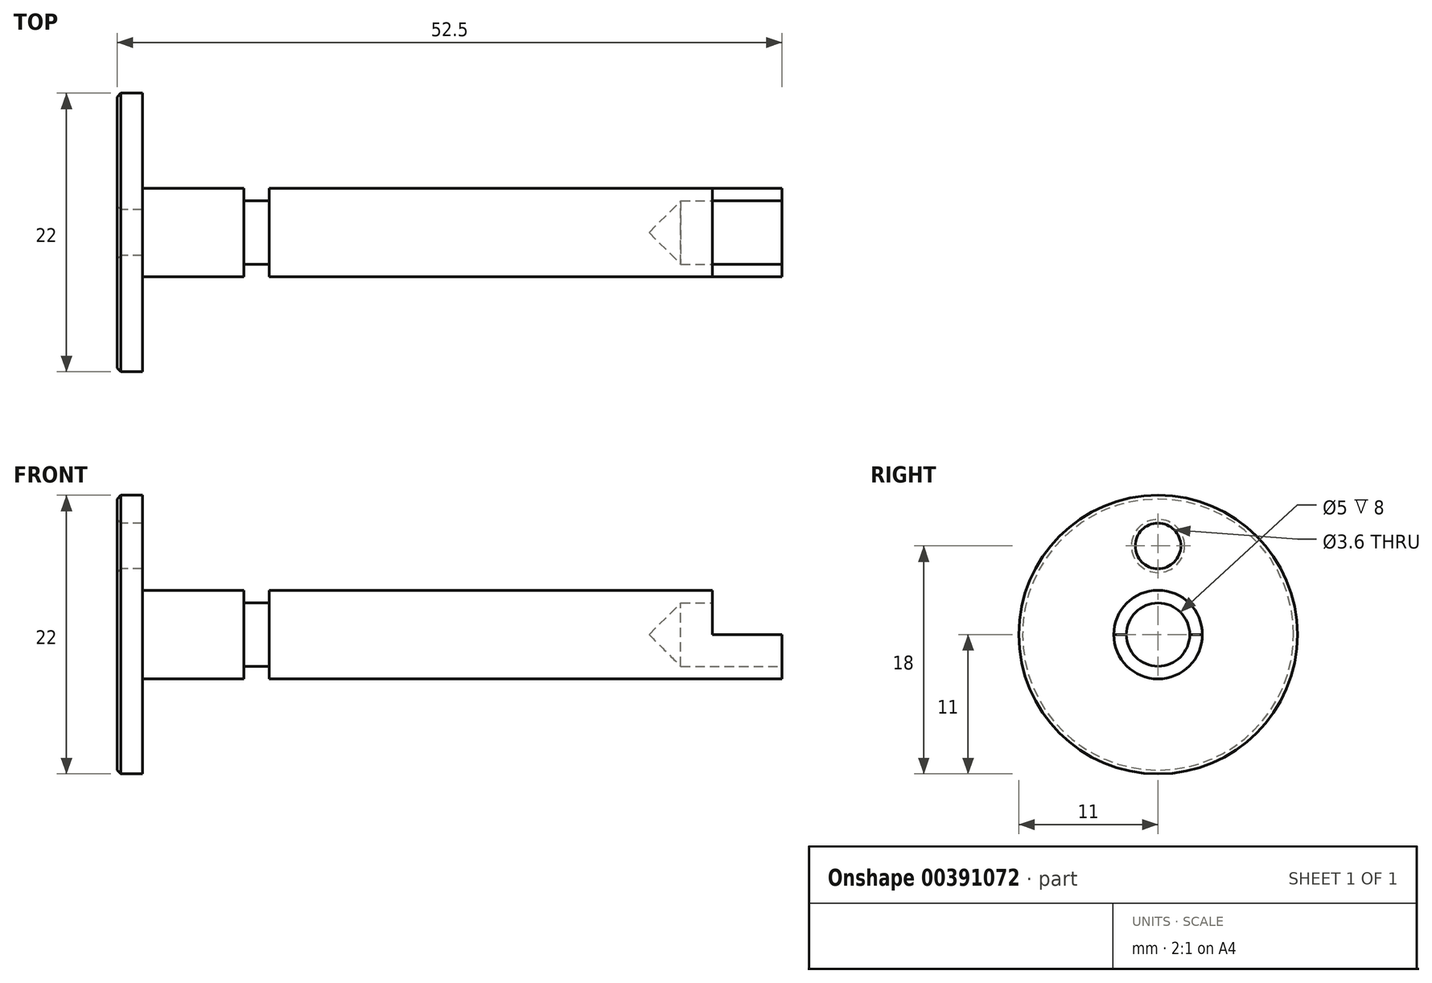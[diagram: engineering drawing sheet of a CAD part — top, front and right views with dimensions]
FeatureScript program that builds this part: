
annotation { "Feature Type Name" : "Feature", "Feature Type Description" : "" }
export const myFeature = defineFeature(function(context is Context, id is Id, definition is map)
    precondition{}
    {
        {
            var Q0;
            Q0=qCreatedBy(makeId("Front.planeOp"),FACE);
            var sketch = newSketch(context, id + "F0", { "sketchPlane" : qUnion([Q0])});
            skLineSegment(sketch, "E0", {"start": v(0, 0) * mm, "end": v(0, 11) * mm});
            skLineSegment(sketch, "E1", {"start": v(0, 11) * mm, "end": v(2, 11) * mm});
            skLineSegment(sketch, "E2", {"start": v(2, 11) * mm, "end": v(2, 3.5) * mm});
            skLineSegment(sketch, "E3", {"start": v(2, 3.5) * mm, "end": v(10, 3.5) * mm});
            skLineSegment(sketch, "E4", {"start": v(10, 3.5) * mm, "end": v(10, 2.5) * mm});
            skLineSegment(sketch, "E5", {"start": v(10, 2.5) * mm, "end": v(12, 2.5) * mm});
            skLineSegment(sketch, "E6", {"start": v(12, 2.5) * mm, "end": v(12, 3.5) * mm});
            skLineSegment(sketch, "E7", {"start": v(12, 3.5) * mm, "end": v(52.5, 3.5) * mm});
            skLineSegment(sketch, "E8", {"start": v(52.5, 3.5) * mm, "end": v(52.5, 2.5) * mm});
            skLineSegment(sketch, "E9", {"start": v(52.5, 2.5) * mm, "end": v(44.5, 2.5) * mm});
            skLineSegment(sketch, "E10", {"start": v(42, 0) * mm, "end": v(0, 0) * mm});
            skLineSegment(sketch, "E11", {"start": v(44.5, 2.5) * mm, "end": v(42, 0) * mm});
            skPoint(sketch, "E12.end.orphan", {"position": v(44.5, 0) * mm});
            skSolve(sketch);
        }
        {
            var Q0;
            Q0 = qSketchRegion(id + "F0", true);
            var Q1;
            Q1=sQuery(id+"F0.wireOp",EDGE,"E10");
            revolve(context, id + "F1", {"surfaceOperationType" : NewSurfaceOperationType.NEW, "entities" : qUnion([Q0]), "axis" : qUnion([Q1]), "revolveType" : RevolveType.FULL});
        }
        {
            var Q0;
            Q0=makeQuery(id+"F1.opRevolve","SWEPT_FACE",FACE,{"disambiguationData":[OSD([sQuery(id+"F0.wireOp",EDGE,"E8")])]});
            var sketch = newSketch(context, id + "F2", { "sketchPlane" : qUnion([Q0])});
            skArc(sketch, "E13.0", {"start": v(3.5, 0) * mm, "mid": v(0, 3.5) * mm, "end": v(-3.5, 0) * mm});
            skArc(sketch, "E14.0", {"start": v(2.5, 0) * mm, "mid": v(0, 2.5) * mm, "end": v(-2.5, 0) * mm});
            skLineSegment(sketch, "E15", {"start": v(-3.5, 0) * mm, "end": v(-2.5, 0) * mm});
            skLineSegment(sketch, "E16.trimOffspring", {"start": v(2.5, 0) * mm, "end": v(3.5, 0) * mm});
            skSolve(sketch);
        }
        {
            var Q0;
            Q0=makeQuery(id+"F2.imprint","IMPRINT",FACE,{"disambiguationData":[TD([[makeQuery(id+"F2.imprint","IMPRINT",EDGE,{"derivedFrom":sQuery(id+"F2.wireOp",EDGE,"E13.0")}),1.0]])]});
            extrude(context, id + "F3", {"entities" : qUnion([Q0]), "operationType" : NewBodyOperationType.REMOVE, "oppositeDirection" : true, "depth" : 5.5 * mm, "offsetDistance" : 25 * mm});
        }
        {
            var Q0;
            Q0=makeQuery(id+"F1.opRevolve","SWEPT_FACE",FACE,{"disambiguationData":[OSD([sQuery(id+"F0.wireOp",EDGE,"E0")])]});
            var sketch = newSketch(context, id + "F4", { "sketchPlane" : qUnion([Q0])});
            skPoint(sketch, "E17", {"position": v(0, 7) * mm});
            skSolve(sketch);
        }
        {
            var Q0;
            Q0=sQuery(id+"F4.wireOp",VERTEX,"E17");
            var Q1;
            Q1=makeQuery(id+"F1.opRevolve","SWEPT_BODY",BODY,{"disambiguationData":[OSD([sQuery(id+"F0.wireOp",EDGE,"E0"),sQuery(id+"F0.wireOp",EDGE,"E1"),sQuery(id+"F0.wireOp",EDGE,"E2"),sQuery(id+"F0.wireOp",EDGE,"E3"),sQuery(id+"F0.wireOp",EDGE,"E4"),sQuery(id+"F0.wireOp",EDGE,"E5"),sQuery(id+"F0.wireOp",EDGE,"E6"),sQuery(id+"F0.wireOp",EDGE,"E7"),sQuery(id+"F0.wireOp",EDGE,"E8"),sQuery(id+"F0.wireOp",EDGE,"E9"),sQuery(id+"F0.wireOp",EDGE,"E10"),sQuery(id+"F0.wireOp",EDGE,"E11")])]});
            hole(context, id + "F5", {"style" : HoleStyle.SIMPLE, "endStyle" : HoleEndStyle.THROUGH, "holeDiameter" : 3.6 * mm, "majorDiameter" : 5 * mm, "isTappedThrough" : true, "tappedDepth" : 100 * mm, "tapClearance" : 3, "startFromSketch" : true, "locations" : qUnion([Q0]), "scope" : qUnion([Q1])});
        }
        {
            var Q0;
            Q0=makeQuery(id+"F1.opRevolve","SWEPT_FACE",FACE,{"disambiguationData":[OSD([sQuery(id+"F0.wireOp",EDGE,"E0")])]});
            chamfer(context, id + "F6", {"entities" : qUnion([Q0]), "width" : .3 * mm, "tangentPropagation" : true});
        }
    });
